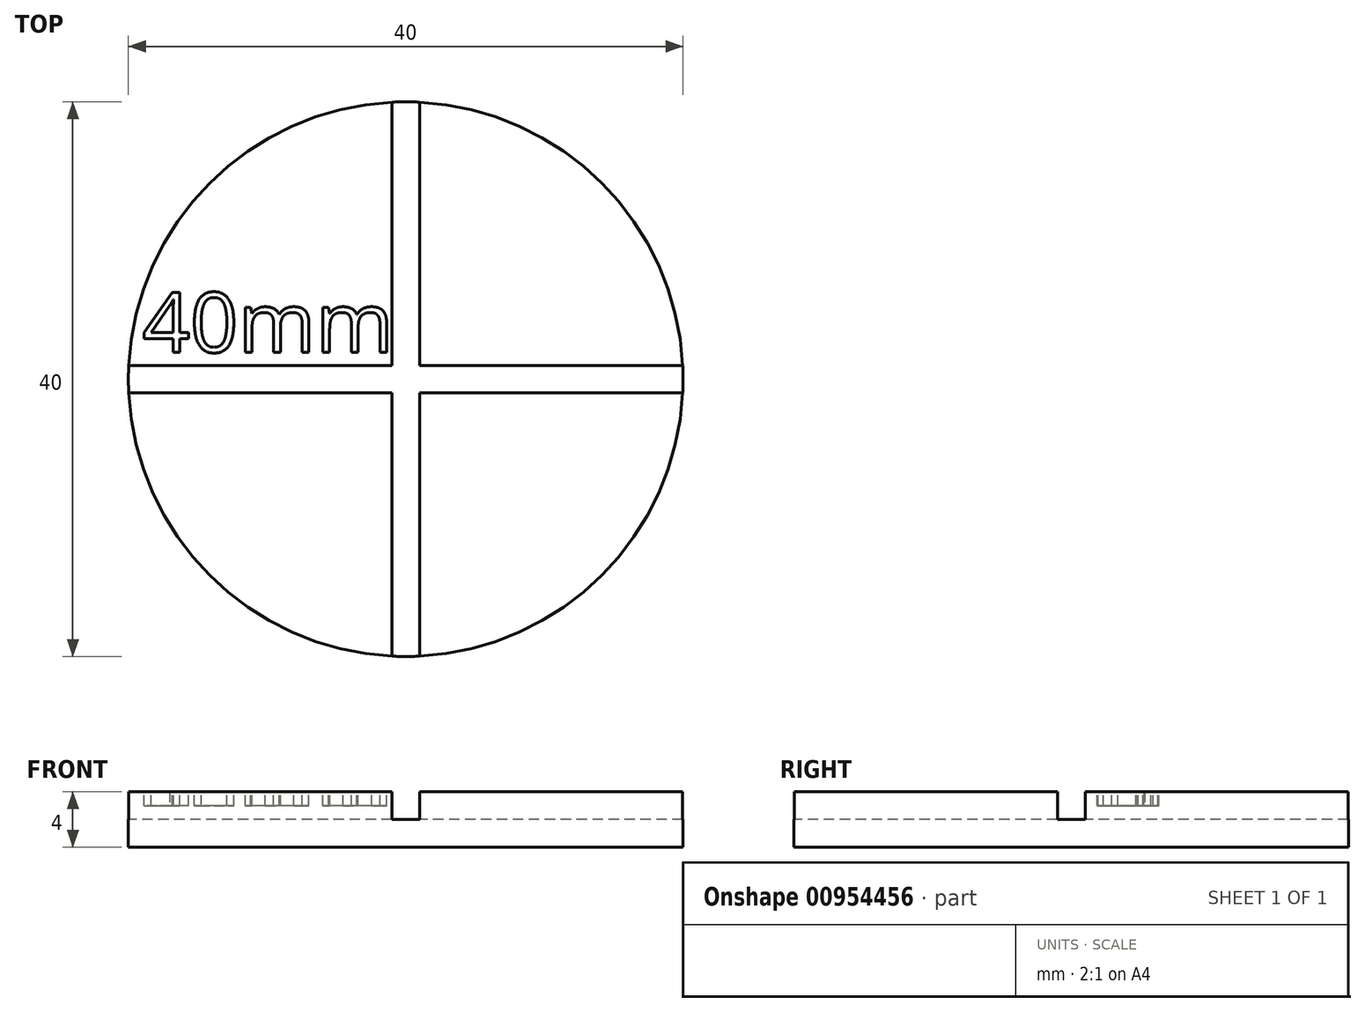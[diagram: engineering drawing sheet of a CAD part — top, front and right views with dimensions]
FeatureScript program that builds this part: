
annotation { "Feature Type Name" : "Feature", "Feature Type Description" : "" }
export const myFeature = defineFeature(function(context is Context, id is Id, definition is map)
    precondition{}
    {
        {
            var Q0;
            Q0=qCreatedBy(makeId("Top.planeOp"),FACE);
            var sketch = newSketch(context, id + "F0", { "sketchPlane" : qUnion([Q0])});
            skCircle(sketch, "E0", {"center": v(0, 0) * mm, "radius": 20 * mm});
            skSolve(sketch);
        }
        {
            var Q0;
            Q0=qSketchRegion(id+"F0",true);
            extrude(context, id + "F1", {"entities" : qUnion([Q0]), "depth" : 4 * mm, "offsetDistance" : 25 * mm});
        }
        {
            var Q0;
            Q0=makeQuery(id+"F1.opExtrude","CAP_FACE",FACE,{"disambiguationData":[OSD([sQuery(id+"F0.wireOp",EDGE,"E0")])],"isStart":false});
            var sketch = newSketch(context, id + "F2", { "sketchPlane" : qUnion([Q0])});
            skLineSegment(sketch, "E1.bottom", {"start": v(25, -1) * mm, "end": v(-25, -1) * mm});
            skLineSegment(sketch, "E1.top", {"start": v(25, 1) * mm, "end": v(-25, 1) * mm});
            skLineSegment(sketch, "E1.left", {"start": v(25, -1) * mm, "end": v(25, 1) * mm});
            skLineSegment(sketch, "E1.right", {"start": v(-25, -1) * mm, "end": v(-25, 1) * mm});
            skPoint(sketch, "E1.middle", {"position": v(0, 0) * mm});
            skLineSegment(sketch, "E2.bottom", {"start": v(-1, 25) * mm, "end": v(1, 25) * mm});
            skLineSegment(sketch, "E2.top", {"start": v(-1, -25) * mm, "end": v(1, -25) * mm});
            skLineSegment(sketch, "E2.left", {"start": v(-1, 25) * mm, "end": v(-1, -25) * mm});
            skLineSegment(sketch, "E2.right", {"start": v(1, 25) * mm, "end": v(1, -25) * mm});
            skSolve(sketch);
        }
        {
            var Q0;
            Q0=qSketchRegion(id+"F2",true);
            extrude(context, id + "F3", {"entities" : qUnion([Q0]), "operationType" : NewBodyOperationType.REMOVE, "oppositeDirection" : true, "depth" : 2 * mm, "offsetDistance" : 25 * mm});
        }
        {
            var Q0;
            {var subQ0=sQuery(id+"F0.wireOp",EDGE,"E0");var subQ1=sQuery(id+"F2.wireOp",EDGE,"E1.top");var subQ4=sQuery(id+"F2.wireOp",EDGE,"E2.left");var subQ5=makeQuery(id+"F2.imprint","INTERSECT",VERTEX,{"derivedFrom":[subQ1,subQ4]});Q0=makeQuery(id+"F3.boolean.opBoolean","SPLIT",FACE,{"disambiguationData":[TD([makeQuery(id+"F3.opExtrude","SWEPT_FACE",FACE,{"disambiguationData":[OSD([subQ1]),TDD([makeQuery(id+"F2.imprint","IMPRINT",EDGE,{"disambiguationData":[TD([[subQ5,-1.0]])],"derivedFrom":subQ1}),makeQuery(id+"F2.imprint","IMPRINT",EDGE,{"disambiguationData":[TD([[makeQuery(id+"F2.imprint","INTERSECT",VERTEX,{"derivedFrom":[subQ1,sQuery(id+"F2.wireOp",EDGE,"E1.right")]}),1.0]])],"derivedFrom":subQ1})])]})])],"derivedFrom":makeQuery(id+"F1.opExtrude","CAP_FACE",FACE,{"disambiguationData":[OSD([subQ0])],"isStart":false})});}
            var sketch = newSketch(context, id + "F4", { "sketchPlane" : qUnion([Q0])});
            skText(sketch, "E3", { "text": "40mm", "fontName": "OpenSans-Regular.ttf"});
            const initialGuessF4  = {"E3": [-0.01899, 0.00194, 1, 0, 0.00434]};
            skSetInitialGuess(sketch, initialGuessF4);
            skSolve(sketch);
        }
        {
            var Q0;
            Q0 = qSketchRegion(id + "F4", true);
            extrude(context, id + "F5", {"entities" : qUnion([Q0]), "operationType" : NewBodyOperationType.REMOVE, "oppositeDirection" : true, "depth" : 1 * mm, "offsetDistance" : 25 * mm});
        }
    });
